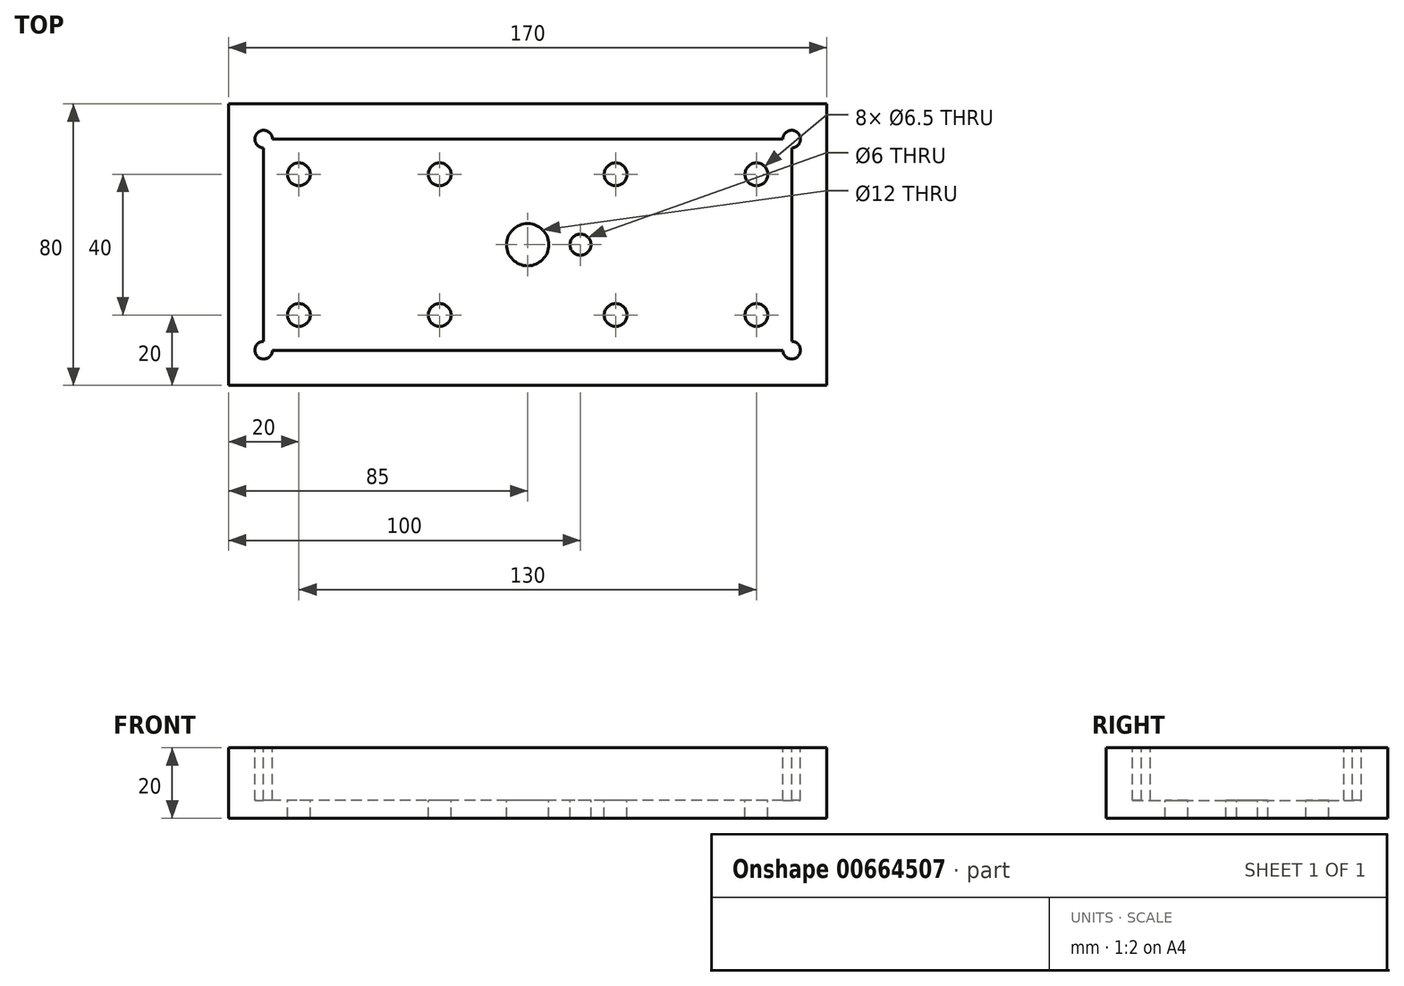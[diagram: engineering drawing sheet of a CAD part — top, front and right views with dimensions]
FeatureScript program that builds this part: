
annotation { "Feature Type Name" : "Feature", "Feature Type Description" : "" }
export const myFeature = defineFeature(function(context is Context, id is Id, definition is map)
    precondition{}
    {
        {
            var Q0;
            Q0=qCreatedBy(makeId("Top.planeOp"),FACE);
            var sketch = newSketch(context, id + "F0", { "sketchPlane" : qUnion([Q0])});
            skLineSegment(sketch, "E0.bottom", {"start": v(85, -40) * mm, "end": v(-85, -40) * mm});
            skLineSegment(sketch, "E0.top", {"start": v(85, 40) * mm, "end": v(-85, 40) * mm});
            skLineSegment(sketch, "E0.left", {"start": v(85, -40) * mm, "end": v(85, 40) * mm});
            skLineSegment(sketch, "E0.right", {"start": v(-85, -40) * mm, "end": v(-85, 40) * mm});
            skPoint(sketch, "E0.middle", {"position": v(0, 0) * mm});
            skSolve(sketch);
        }
        {
            var Q0;
            Q0 = qSketchRegion(id + "F0", true);
            extrude(context, id + "F1", {"entities" : qUnion([Q0]), "depth" : 10 * mm, "offsetDistance" : 25 * mm});
        }
        {
            var Q0;
            Q0=makeQuery(id+"F1.opExtrude","CAP_FACE",FACE,{"disambiguationData":[OSD([sQuery(id+"F0.wireOp",EDGE,"E0.bottom"),sQuery(id+"F0.wireOp",EDGE,"E0.top"),sQuery(id+"F0.wireOp",EDGE,"E0.left"),sQuery(id+"F0.wireOp",EDGE,"E0.right")])],"isStart":false});
            var sketch = newSketch(context, id + "F2", { "sketchPlane" : qUnion([Q0])});
            skLineSegment(sketch, "E1.bottom", {"start": v(75, -30) * mm, "end": v(-75, -30) * mm});
            skLineSegment(sketch, "E1.top", {"start": v(75, 30) * mm, "end": v(-75, 30) * mm});
            skLineSegment(sketch, "E1.left", {"start": v(75, -30) * mm, "end": v(75, 30) * mm});
            skLineSegment(sketch, "E1.right", {"start": v(-75, -30) * mm, "end": v(-75, 30) * mm});
            skPoint(sketch, "E1.middle", {"position": v(0, 0) * mm});
            skSolve(sketch);
        }
        {
            var Q0;
            Q0 = qSketchRegion(id + "F2", true);
            extrude(context, id + "F3", {"entities" : qUnion([Q0]), "operationType" : NewBodyOperationType.REMOVE, "oppositeDirection" : true, "depth" : 5 * mm, "offsetDistance" : 25 * mm});
        }
        {
            var Q0;
            Q0=makeQuery(id+"F1.opExtrude","CAP_FACE",FACE,{"disambiguationData":[OSD([sQuery(id+"F0.wireOp",EDGE,"E0.bottom"),sQuery(id+"F0.wireOp",EDGE,"E0.top"),sQuery(id+"F0.wireOp",EDGE,"E0.left"),sQuery(id+"F0.wireOp",EDGE,"E0.right")])],"isStart":false});
            var sketch = newSketch(context, id + "F4", { "sketchPlane" : qUnion([Q0])});
            skCircle(sketch, "E2", {"center": v(75, 30) * mm, "radius": 2.5 * mm});
            skCircle(sketch, "E3", {"center": v(75, -30) * mm, "radius": 2.5 * mm});
            skCircle(sketch, "E4", {"center": v(-75, 30) * mm, "radius": 2.5 * mm});
            skCircle(sketch, "E5", {"center": v(-75, -30) * mm, "radius": 2.5 * mm});
            skLineSegment(sketch, "E6", {"start": v(-75, 30) * mm, "end": v(-75, 27.5) * mm});
            skLineSegment(sketch, "E7", {"start": v(-75, 27.5) * mm, "end": v(-75, 30) * mm});
            skLineSegment(sketch, "E8", {"start": v(-75, 30) * mm, "end": v(-72.5, 30) * mm});
            skLineSegment(sketch, "E9", {"start": v(-75, -30) * mm, "end": v(-72.5, -30) * mm});
            skLineSegment(sketch, "E10", {"start": v(-75, -30) * mm, "end": v(-75, -27.5) * mm});
            skLineSegment(sketch, "E11", {"start": v(75, 30) * mm, "end": v(75, 27.5) * mm});
            skLineSegment(sketch, "E12", {"start": v(75, 30) * mm, "end": v(72.5, 30) * mm});
            skLineSegment(sketch, "E13", {"start": v(75, -30) * mm, "end": v(72.5, -30) * mm});
            skLineSegment(sketch, "E14", {"start": v(75, -30) * mm, "end": v(75, -27.5) * mm});
            skSolve(sketch);
        }
        {
            var Q0;
            Q0 = qSketchRegion(id + "F4", true);
            extrude(context, id + "F5", {"entities" : qUnion([Q0]), "operationType" : NewBodyOperationType.REMOVE, "oppositeDirection" : true, "depth" : 5 * mm, "offsetDistance" : 25 * mm});
        }
        {
            var Q0;
            Q0=makeQuery(id+"F5.boolean.opBoolean","MERGE",FACE,{"derivedFrom":[makeQuery(id+"F3.boolean.opBoolean","COPY",FACE,{"derivedFrom":makeQuery(id+"F3.opExtrude","CAP_FACE",FACE,{"disambiguationData":[OSD([sQuery(id+"F2.wireOp",EDGE,"E1.bottom"),sQuery(id+"F2.wireOp",EDGE,"E1.top"),sQuery(id+"F2.wireOp",EDGE,"E1.left"),sQuery(id+"F2.wireOp",EDGE,"E1.right")])],"isStart":false})})],"fromTools":[makeQuery(id+"F5.opExtrude","CAP_FACE",FACE,{"disambiguationData":[OSD([sQuery(id+"F4.wireOp",EDGE,"E2")])],"isStart":false}),makeQuery(id+"F5.opExtrude","CAP_FACE",FACE,{"disambiguationData":[OSD([sQuery(id+"F4.wireOp",EDGE,"E3")])],"isStart":false}),makeQuery(id+"F5.opExtrude","CAP_FACE",FACE,{"disambiguationData":[OSD([sQuery(id+"F4.wireOp",EDGE,"E4")])],"isStart":false}),makeQuery(id+"F5.opExtrude","CAP_FACE",FACE,{"disambiguationData":[OSD([sQuery(id+"F4.wireOp",EDGE,"E5")])],"isStart":false})]});
            var sketch = newSketch(context, id + "F6", { "sketchPlane" : qUnion([Q0])});
            skCircle(sketch, "E15", {"center": v(0, 0) * mm, "radius": 6 * mm});
            skLineSegment(sketch, "E16", {"start": v(0, 0) * mm, "end": v(15, 0) * mm});
            skCircle(sketch, "E17", {"center": v(15, 0) * mm, "radius": 3 * mm});
            skLineSegment(sketch, "E18.bottom", {"start": v(65, -20) * mm, "end": v(-65, -20) * mm});
            skLineSegment(sketch, "E18.top", {"start": v(65, 20) * mm, "end": v(-65, 20) * mm});
            skLineSegment(sketch, "E18.left", {"start": v(65, -20) * mm, "end": v(65, 20) * mm});
            skLineSegment(sketch, "E18.right", {"start": v(-65, -20) * mm, "end": v(-65, 20) * mm});
            skCircle(sketch, "E19", {"center": v(65, 20) * mm, "radius": 3.25 * mm});
            skCircle(sketch, "E20", {"center": v(65, -20) * mm, "radius": 3.25 * mm});
            skCircle(sketch, "E21", {"center": v(-65, 20) * mm, "radius": 3.25 * mm});
            skCircle(sketch, "E22", {"center": v(-65, -20) * mm, "radius": 3.25 * mm});
            skLineSegment(sketch, "E23", {"start": v(-65, 0) * mm, "end": v(-25, 0) * mm});
            skLineSegment(sketch, "E24", {"start": v(65, 0) * mm, "end": v(25, 0) * mm});
            skCircle(sketch, "E25", {"center": v(25, -20) * mm, "radius": 3.25 * mm});
            skCircle(sketch, "E26", {"center": v(25, 20) * mm, "radius": 3.25 * mm});
            skCircle(sketch, "E27", {"center": v(-25, -20) * mm, "radius": 3.25 * mm});
            skCircle(sketch, "E28", {"center": v(-25, 20) * mm, "radius": 3.25 * mm});
            skSolve(sketch);
        }
        {
            var Q0;
            {var subQ0=sQuery(id+"F6.wireOp",EDGE,"E18.right");var subQ1=sQuery(id+"F6.wireOp",EDGE,"E18.bottom");var subQ2=makeQuery(id+"F6.imprint","INTERSECT",VERTEX,{"derivedFrom":[subQ1,subQ0]});Q0=makeQuery(id+"F6.imprint","IMPRINT",FACE,{"disambiguationData":[TD([[makeQuery(id+"F6.imprint","IMPRINT",EDGE,{"disambiguationData":[TD([[subQ2,1.0]])],"derivedFrom":subQ1}),-1.0]])]});}
            var Q1;
            {var subQ0=sQuery(id+"F6.wireOp",EDGE,"E18.left");var subQ1=sQuery(id+"F6.wireOp",EDGE,"E18.top");var subQ2=makeQuery(id+"F6.imprint","INTERSECT",VERTEX,{"derivedFrom":[subQ1,subQ0]});Q1=makeQuery(id+"F6.imprint","IMPRINT",FACE,{"disambiguationData":[TD([[makeQuery(id+"F6.imprint","IMPRINT",EDGE,{"disambiguationData":[TD([[subQ2,-1.0]])],"derivedFrom":subQ1}),-1.0]])]});}
            var Q2;
            {var subQ0=sQuery(id+"F6.wireOp",EDGE,"E26");var subQ1=sQuery(id+"F6.wireOp",EDGE,"E18.top");var subQ2=makeQuery(id+"F6.imprint","INTERSECT",VERTEX,{"disambiguationData":[OD(0.0)],"derivedFrom":[subQ1,subQ0]});Q2=makeQuery(id+"F6.imprint","IMPRINT",FACE,{"disambiguationData":[TD([[makeQuery(id+"F6.imprint","IMPRINT",EDGE,{"disambiguationData":[TD([[subQ2,-1.0]])],"derivedFrom":subQ1}),1.0]])]});}
            var Q3;
            {var subQ0=sQuery(id+"F6.wireOp",EDGE,"E27");var subQ1=sQuery(id+"F6.wireOp",EDGE,"E18.bottom");var subQ2=makeQuery(id+"F6.imprint","INTERSECT",VERTEX,{"disambiguationData":[OD(0.0)],"derivedFrom":[subQ1,subQ0]});Q3=makeQuery(id+"F6.imprint","IMPRINT",FACE,{"disambiguationData":[TD([[makeQuery(id+"F6.imprint","IMPRINT",EDGE,{"disambiguationData":[TD([[subQ2,-1.0]])],"derivedFrom":subQ1}),-1.0]])]});}
            var Q4;
            {var subQ0=sQuery(id+"F6.wireOp",EDGE,"E28");var subQ1=sQuery(id+"F6.wireOp",EDGE,"E18.top");var subQ2=makeQuery(id+"F6.imprint","INTERSECT",VERTEX,{"disambiguationData":[OD(0.0)],"derivedFrom":[subQ1,subQ0]});Q4=makeQuery(id+"F6.imprint","IMPRINT",FACE,{"disambiguationData":[TD([[makeQuery(id+"F6.imprint","IMPRINT",EDGE,{"disambiguationData":[TD([[subQ2,-1.0]])],"derivedFrom":subQ1}),-1.0]])]});}
            var Q5;
            {var subQ0=sQuery(id+"F6.wireOp",EDGE,"E18.right");var subQ1=sQuery(id+"F6.wireOp",EDGE,"E18.top");var subQ2=makeQuery(id+"F6.imprint","INTERSECT",VERTEX,{"derivedFrom":[subQ1,subQ0]});Q5=makeQuery(id+"F6.imprint","IMPRINT",FACE,{"disambiguationData":[TD([[makeQuery(id+"F6.imprint","IMPRINT",EDGE,{"disambiguationData":[TD([[subQ2,1.0]])],"derivedFrom":subQ1}),-1.0]])]});}
            var Q6;
            {var subQ0=sQuery(id+"F6.wireOp",EDGE,"E18.right");var subQ1=sQuery(id+"F6.wireOp",EDGE,"E18.bottom");var subQ2=makeQuery(id+"F6.imprint","INTERSECT",VERTEX,{"derivedFrom":[subQ1,subQ0]});Q6=makeQuery(id+"F6.imprint","IMPRINT",FACE,{"disambiguationData":[TD([[makeQuery(id+"F6.imprint","IMPRINT",EDGE,{"disambiguationData":[TD([[subQ2,1.0]])],"derivedFrom":subQ1}),1.0]])]});}
            var Q7;
            {var subQ0=sQuery(id+"F6.wireOp",EDGE,"E25");var subQ1=sQuery(id+"F6.wireOp",EDGE,"E18.bottom");var subQ2=makeQuery(id+"F6.imprint","INTERSECT",VERTEX,{"disambiguationData":[OD(0.0)],"derivedFrom":[subQ1,subQ0]});Q7=makeQuery(id+"F6.imprint","IMPRINT",FACE,{"disambiguationData":[TD([[makeQuery(id+"F6.imprint","IMPRINT",EDGE,{"disambiguationData":[TD([[subQ2,-1.0]])],"derivedFrom":subQ1}),-1.0]])]});}
            var Q8;
            {var subQ0=sQuery(id+"F6.wireOp",EDGE,"E18.right");var subQ1=sQuery(id+"F6.wireOp",EDGE,"E18.top");var subQ2=makeQuery(id+"F6.imprint","INTERSECT",VERTEX,{"derivedFrom":[subQ1,subQ0]});Q8=makeQuery(id+"F6.imprint","IMPRINT",FACE,{"disambiguationData":[TD([[makeQuery(id+"F6.imprint","IMPRINT",EDGE,{"disambiguationData":[TD([[subQ2,1.0]])],"derivedFrom":subQ1}),1.0]])]});}
            var Q9;
            {var subQ0=sQuery(id+"F6.wireOp",EDGE,"E27");var subQ1=sQuery(id+"F6.wireOp",EDGE,"E18.bottom");var subQ2=makeQuery(id+"F6.imprint","INTERSECT",VERTEX,{"disambiguationData":[OD(0.0)],"derivedFrom":[subQ1,subQ0]});Q9=makeQuery(id+"F6.imprint","IMPRINT",FACE,{"disambiguationData":[TD([[makeQuery(id+"F6.imprint","IMPRINT",EDGE,{"disambiguationData":[TD([[subQ2,-1.0]])],"derivedFrom":subQ1}),1.0]])]});}
            var Q10;
            {var subQ0=sQuery(id+"F6.wireOp",EDGE,"E28");var subQ1=sQuery(id+"F6.wireOp",EDGE,"E18.top");var subQ2=makeQuery(id+"F6.imprint","INTERSECT",VERTEX,{"disambiguationData":[OD(0.0)],"derivedFrom":[subQ1,subQ0]});Q10=makeQuery(id+"F6.imprint","IMPRINT",FACE,{"disambiguationData":[TD([[makeQuery(id+"F6.imprint","IMPRINT",EDGE,{"disambiguationData":[TD([[subQ2,-1.0]])],"derivedFrom":subQ1}),1.0]])]});}
            var Q11;
            {var subQ0=sQuery(id+"F6.wireOp",EDGE,"E18.left");var subQ1=sQuery(id+"F6.wireOp",EDGE,"E18.bottom");var subQ2=makeQuery(id+"F6.imprint","INTERSECT",VERTEX,{"derivedFrom":[subQ1,subQ0]});Q11=makeQuery(id+"F6.imprint","IMPRINT",FACE,{"disambiguationData":[TD([[makeQuery(id+"F6.imprint","IMPRINT",EDGE,{"disambiguationData":[TD([[subQ2,-1.0]])],"derivedFrom":subQ1}),1.0]])]});}
            var Q12;
            {var subQ0=sQuery(id+"F6.wireOp",EDGE,"E18.left");var subQ1=sQuery(id+"F6.wireOp",EDGE,"E18.bottom");var subQ2=makeQuery(id+"F6.imprint","INTERSECT",VERTEX,{"derivedFrom":[subQ1,subQ0]});Q12=makeQuery(id+"F6.imprint","IMPRINT",FACE,{"disambiguationData":[TD([[makeQuery(id+"F6.imprint","IMPRINT",EDGE,{"disambiguationData":[TD([[subQ2,-1.0]])],"derivedFrom":subQ1}),-1.0]])]});}
            var Q13;
            {var subQ0=sQuery(id+"F6.wireOp",EDGE,"E18.left");var subQ1=sQuery(id+"F6.wireOp",EDGE,"E18.top");var subQ2=makeQuery(id+"F6.imprint","INTERSECT",VERTEX,{"derivedFrom":[subQ1,subQ0]});Q13=makeQuery(id+"F6.imprint","IMPRINT",FACE,{"disambiguationData":[TD([[makeQuery(id+"F6.imprint","IMPRINT",EDGE,{"disambiguationData":[TD([[subQ2,-1.0]])],"derivedFrom":subQ1}),1.0]])]});}
            var Q14;
            {var subQ0=sQuery(id+"F6.wireOp",EDGE,"E25");var subQ1=sQuery(id+"F6.wireOp",EDGE,"E18.bottom");var subQ2=makeQuery(id+"F6.imprint","INTERSECT",VERTEX,{"disambiguationData":[OD(0.0)],"derivedFrom":[subQ1,subQ0]});Q14=makeQuery(id+"F6.imprint","IMPRINT",FACE,{"disambiguationData":[TD([[makeQuery(id+"F6.imprint","IMPRINT",EDGE,{"disambiguationData":[TD([[subQ2,-1.0]])],"derivedFrom":subQ1}),1.0]])]});}
            var Q15;
            {var subQ0=sQuery(id+"F6.wireOp",EDGE,"E26");var subQ1=sQuery(id+"F6.wireOp",EDGE,"E18.top");var subQ2=makeQuery(id+"F6.imprint","INTERSECT",VERTEX,{"disambiguationData":[OD(0.0)],"derivedFrom":[subQ1,subQ0]});Q15=makeQuery(id+"F6.imprint","IMPRINT",FACE,{"disambiguationData":[TD([[makeQuery(id+"F6.imprint","IMPRINT",EDGE,{"disambiguationData":[TD([[subQ2,-1.0]])],"derivedFrom":subQ1}),-1.0]])]});}
            var Q16;
            Q16=makeQuery(id+"F6.imprint","IMPRINT",FACE,{"disambiguationData":[TD([[makeQuery(id+"F6.imprint","IMPRINT",EDGE,{"derivedFrom":sQuery(id+"F6.wireOp",EDGE,"E15")}),1.0]])]});
            var Q17;
            Q17=makeQuery(id+"F6.imprint","IMPRINT",FACE,{"disambiguationData":[TD([[makeQuery(id+"F6.imprint","IMPRINT",EDGE,{"derivedFrom":sQuery(id+"F6.wireOp",EDGE,"E17")}),1.0]])]});
            extrude(context, id + "F7", {"entities" : qUnion([Q0, Q1, Q2, Q3, Q4, Q5, Q6, Q7, Q8, Q9, Q10, Q11, Q12, Q13, Q14, Q15, Q16, Q17]), "operationType" : NewBodyOperationType.REMOVE, "oppositeDirection" : true, "depth" : 5 * mm, "offsetDistance" : 25 * mm});
        }
        {
            var Q0;
            Q0=makeQuery(id+"F1.opExtrude","CAP_FACE",FACE,{"disambiguationData":[OSD([sQuery(id+"F0.wireOp",EDGE,"E0.bottom"),sQuery(id+"F0.wireOp",EDGE,"E0.top"),sQuery(id+"F0.wireOp",EDGE,"E0.left"),sQuery(id+"F0.wireOp",EDGE,"E0.right")])],"isStart":false});
            extrude(context, id + "F8", {"entities" : qUnion([Q0]), "operationType" : NewBodyOperationType.ADD, "depth" : 10 * mm, "offsetDistance" : 25 * mm});
        }
    });
